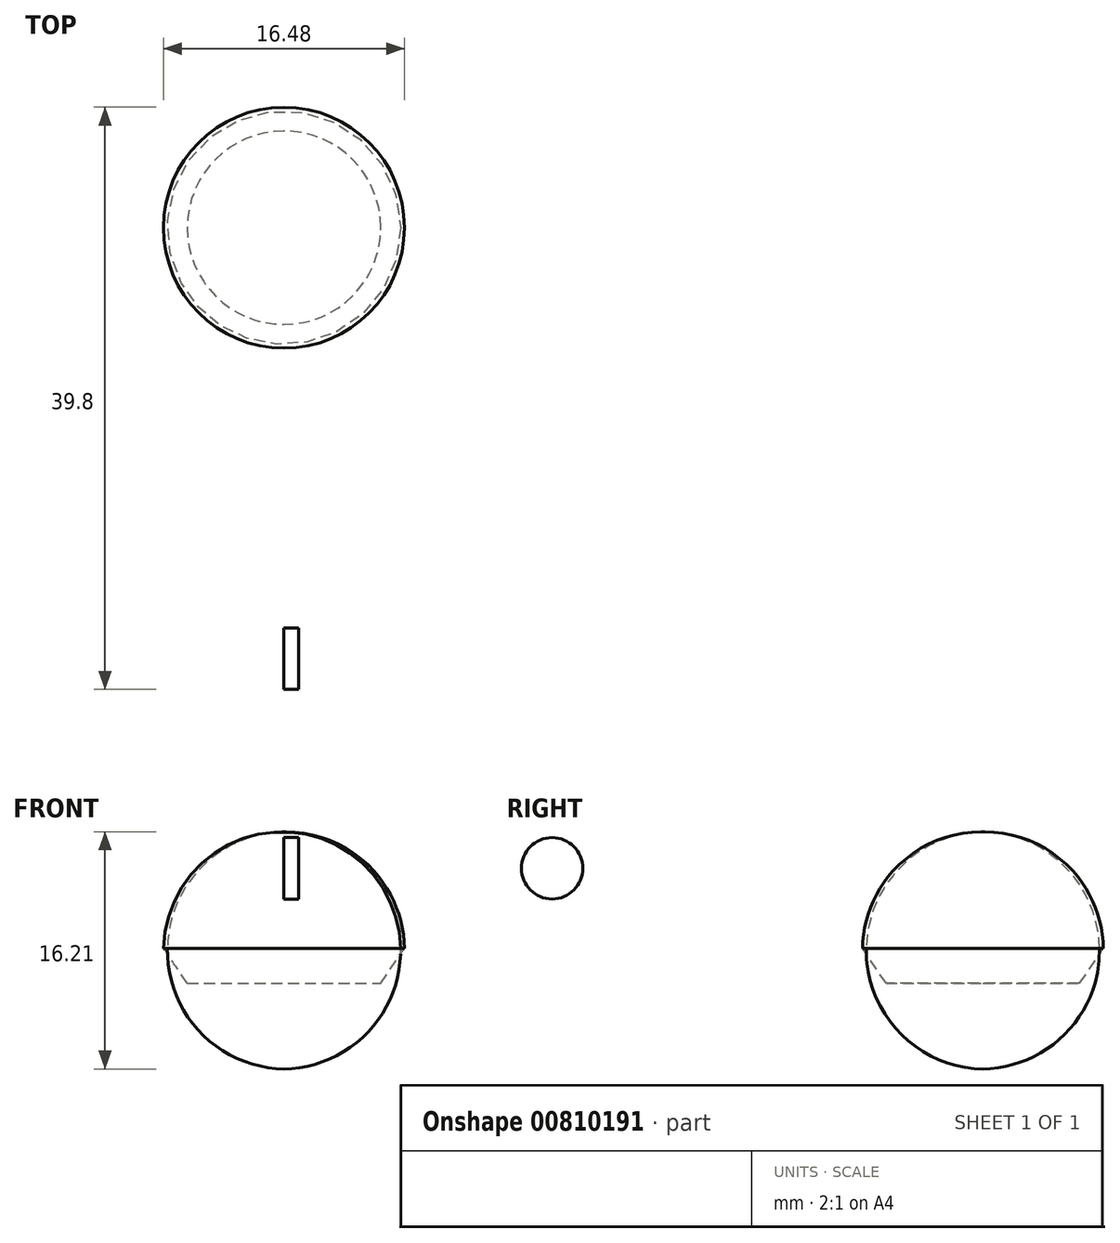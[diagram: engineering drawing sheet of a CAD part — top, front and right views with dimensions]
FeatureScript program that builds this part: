
annotation { "Feature Type Name" : "Feature", "Feature Type Description" : "" }
export const myFeature = defineFeature(function(context is Context, id is Id, definition is map)
    precondition{}
    {
        {
            var Q0;
            Q0=qCreatedBy(makeId("Front.planeOp"),FACE);
            var sketch = newSketch(context, id + "F0", { "sketchPlane" : qUnion([Q0])});
            skLineSegment(sketch, "E0", {"start": v(0, 0) * mm, "end": v(-7.92, 0) * mm});
            skArc(sketch, "E1", {"start": v(0, 10.36) * mm, "mid": v(-6.57, 7.18) * mm, "end": v(-7.92, 0) * mm});
            skLineSegment(sketch, "E2", {"start": v(0, 0) * mm, "end": v(0, 10.36) * mm});
            skSolve(sketch);
        }
        {
            var Q0;
            Q0=makeQuery(id+"F0.imprint","IMPRINT",FACE,{"disambiguationData":[TD([[makeQuery(id+"F0.imprint","IMPRINT",EDGE,{"derivedFrom":sQuery(id+"F0.wireOp",EDGE,"E0")}),-1.0]])]});
            var Q1;
            Q1=sQuery(id+"F0.wireOp",EDGE,"E2");
            revolve(context, id + "F1", {"surfaceOperationType" : NewSurfaceOperationType.NEW, "entities" : qUnion([Q0]), "axis" : qUnion([Q1]), "revolveType" : RevolveType.FULL});
        }
        {
            var Q0;
            Q0=makeQuery(id+"F1.opRevolve","SWEPT_EDGE",EDGE,{"disambiguationData":[OSD([sQuery(id+"F0.wireOp",EDGE,"E0"),sQuery(id+"F0.wireOp",EDGE,"E1")])]});
            chamfer(context, id + "F2", {"entities" : qUnion([Q0]), "chamferType" : ChamferType.TWO_OFFSETS, "width1" : 1 * mm, "oppositeDirection" : false, "width2" : 2 * mm, "tangentPropagation" : true});
        }
        {
            var Q0;
            Q0=qCreatedBy(makeId("Right.planeOp"),FACE);
            var sketch = newSketch(context, id + "F3", { "sketchPlane" : qUnion([Q0])});
            skCircle(sketch, "E3", {"center": v(-29.46, 7.87) * mm, "radius": 2.1 * mm});
            skSolve(sketch);
        }
        {
            var Q0;
            Q0 = qSketchRegion(id + "F3", true);
            extrude(context, id + "F4", {"entities" : qUnion([Q0]), "depth" : 1 * mm, "offsetDistance" : 25 * mm});
        }
    });
